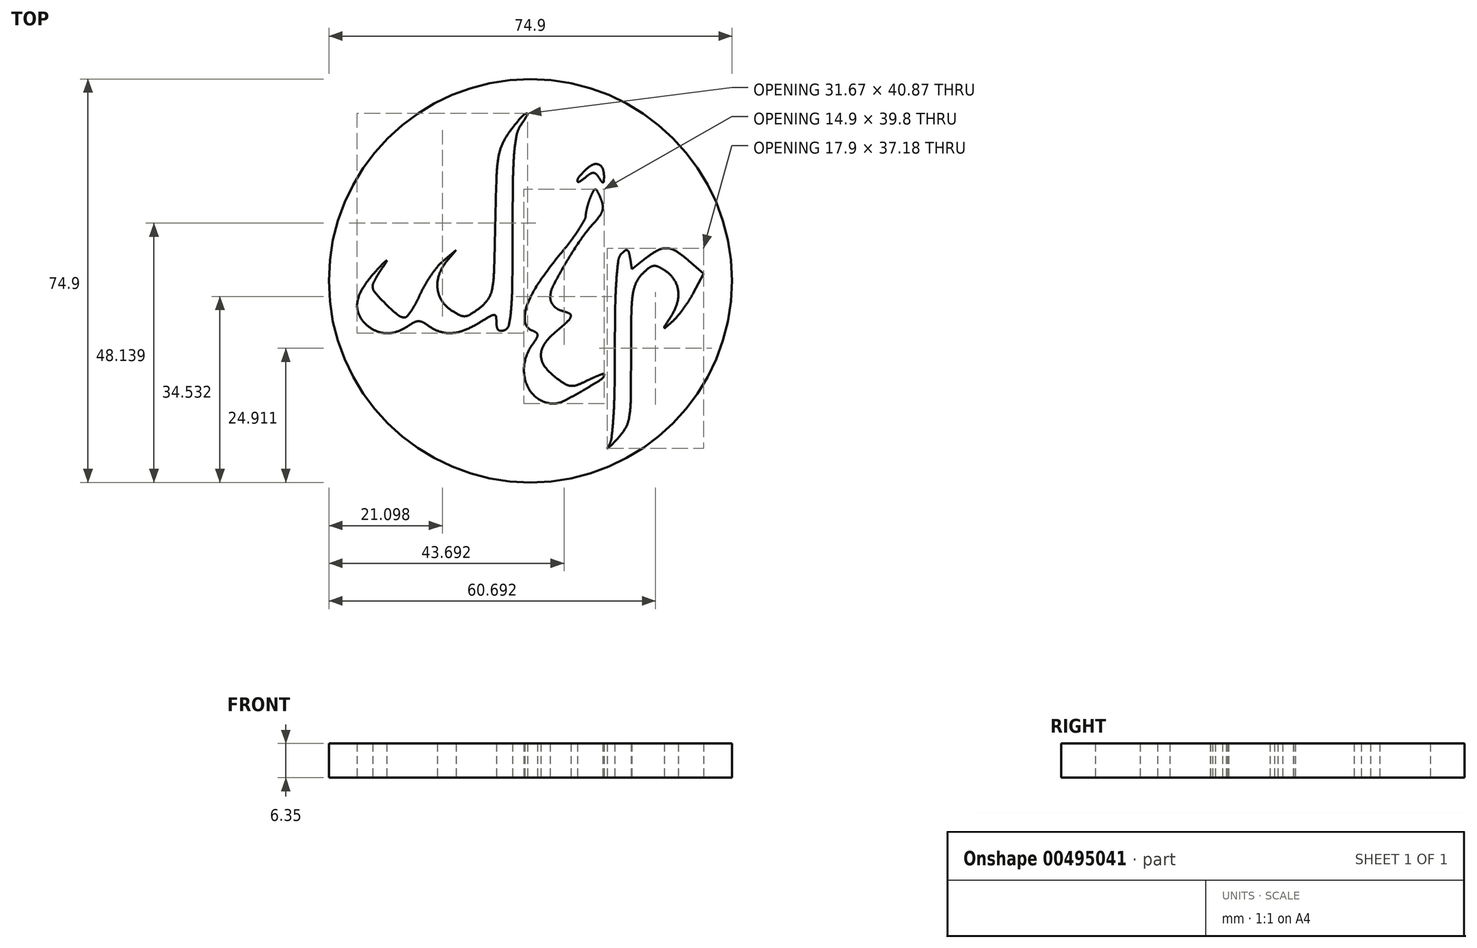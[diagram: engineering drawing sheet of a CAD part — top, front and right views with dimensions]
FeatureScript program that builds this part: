
annotation { "Feature Type Name" : "Feature", "Feature Type Description" : "" }
export const myFeature = defineFeature(function(context is Context, id is Id, definition is map)
    precondition{}
    {
        {
            var Q0;
            Q0=qCreatedBy(makeId("Top.planeOp"),FACE);
            var sketch = newSketch(context, id + "F0", { "sketchPlane" : qUnion([Q0])});
            skArc(sketch, "E0", {"start": v(-3.73, 27.88) * mm, "mid": v(-4.51, 26.73) * mm, "end": v(-5.16, 25.5) * mm});
            skArc(sketch, "E1", {"start": v(-5.16, 25.5) * mm, "mid": v(-5.63, 24.29) * mm, "end": v(-5.92, 23.03) * mm});
            skArc(sketch, "E2", {"start": v(-5.92, 23.03) * mm, "mid": v(-6.17, 21.14) * mm, "end": v(-6.3, 19.24) * mm});
            skArc(sketch, "E3", {"start": v(-6.3, 19.24) * mm, "mid": v(-6.43, 14.99) * mm, "end": v(-6.53, 10.73) * mm});
            skArc(sketch, "E4", {"start": v(-6.53, 10.73) * mm, "mid": v(-6.63, 6.2) * mm, "end": v(-6.76, 1.68) * mm});
            skArc(sketch, "E5", {"start": v(-6.76, 1.68) * mm, "mid": v(-6.88, 0.04) * mm, "end": v(-7.12, -1.59) * mm});
            skArc(sketch, "E6", {"start": v(-7.12, -1.59) * mm, "mid": v(-7.42, -2.58) * mm, "end": v(-7.92, -3.48) * mm});
            skArc(sketch, "E7", {"start": v(-7.92, -3.48) * mm, "mid": v(-8.64, -4.36) * mm, "end": v(-9.5, -5.11) * mm});
            skArc(sketch, "E8", {"start": v(-9.5, -5.11) * mm, "mid": v(-10.33, -5.7) * mm, "end": v(-11.19, -6.27) * mm});
            skArc(sketch, "E9", {"start": v(-11.19, -6.27) * mm, "mid": v(-11.66, -6.5) * mm, "end": v(-12.18, -6.59) * mm});
            skArc(sketch, "E10", {"start": v(-12.18, -6.59) * mm, "mid": v(-12.68, -6.55) * mm, "end": v(-13.15, -6.38) * mm});
            skArc(sketch, "E11", {"start": v(-13.15, -6.38) * mm, "mid": v(-13.96, -5.93) * mm, "end": v(-14.75, -5.45) * mm});
            skArc(sketch, "E12", {"start": v(-14.75, -5.45) * mm, "mid": v(-15.72, -4.65) * mm, "end": v(-16.5, -3.65) * mm});
            skArc(sketch, "E13", {"start": v(-16.5, -3.65) * mm, "mid": v(-17.02, -2.54) * mm, "end": v(-17.27, -1.33) * mm});
            skArc(sketch, "E14", {"start": v(-17.27, -1.33) * mm, "mid": v(-17.24, -0.04) * mm, "end": v(-16.94, 1.22) * mm});
            skArc(sketch, "E15", {"start": v(-16.94, 1.22) * mm, "mid": v(-16.35, 2.47) * mm, "end": v(-15.56, 3.6) * mm});
            skLineSegment(sketch, "E16", {"start": v(-15.56, 3.6) * mm, "end": v(-13.8, 5.68) * mm});
            skLineSegment(sketch, "E17", {"start": v(-13.8, 5.68) * mm, "end": v(-16.2, 3.68) * mm});
            skArc(sketch, "E18", {"start": v(-16.2, 3.68) * mm, "mid": v(-16.76, 3.18) * mm, "end": v(-17.26, 2.62) * mm});
            skArc(sketch, "E19", {"start": v(-17.26, 2.62) * mm, "mid": v(-17.87, 1.83) * mm, "end": v(-18.45, 1.02) * mm});
            skArc(sketch, "E20", {"start": v(-18.45, 1.02) * mm, "mid": v(-19.04, 0.13) * mm, "end": v(-19.6, -0.8) * mm});
            skArc(sketch, "E21", {"start": v(-19.6, -0.8) * mm, "mid": v(-20.07, -1.67) * mm, "end": v(-20.5, -2.57) * mm});
            skArc(sketch, "E22", {"start": v(-20.5, -2.57) * mm, "mid": v(-20.89, -3.39) * mm, "end": v(-21.3, -4.2) * mm});
            skArc(sketch, "E23", {"start": v(-21.3, -4.2) * mm, "mid": v(-21.7, -4.9) * mm, "end": v(-22.14, -5.57) * mm});
            skArc(sketch, "E24", {"start": v(-22.14, -5.57) * mm, "mid": v(-22.51, -6.09) * mm, "end": v(-22.9, -6.59) * mm});
            skArc(sketch, "E25", {"start": v(-22.9, -6.59) * mm, "mid": v(-23.13, -6.76) * mm, "end": v(-23.4, -6.82) * mm});
            skArc(sketch, "E26", {"start": v(-23.4, -6.82) * mm, "mid": v(-24.05, -6.7) * mm, "end": v(-24.62, -6.37) * mm});
            skArc(sketch, "E27", {"start": v(-24.62, -6.37) * mm, "mid": v(-25.74, -5.4) * mm, "end": v(-26.82, -4.37) * mm});
            skArc(sketch, "E28", {"start": v(-26.82, -4.37) * mm, "mid": v(-27.87, -3.3) * mm, "end": v(-28.86, -2.2) * mm});
            skArc(sketch, "E29", {"start": v(-28.86, -2.2) * mm, "mid": v(-29.2, -1.64) * mm, "end": v(-29.3, -1) * mm});
            skArc(sketch, "E30", {"start": v(-29.3, -1) * mm, "mid": v(-29.28, -0.73) * mm, "end": v(-29.2, -0.48) * mm});
            skArc(sketch, "E31", {"start": v(-29.2, -0.48) * mm, "mid": v(-28.95, 0) * mm, "end": v(-28.7, 0.5) * mm});
            skArc(sketch, "E32", {"start": v(-28.7, 0.5) * mm, "mid": v(-28.37, 1.07) * mm, "end": v(-28.02, 1.63) * mm});
            skArc(sketch, "E33", {"start": v(-28.02, 1.63) * mm, "mid": v(-27.63, 2.22) * mm, "end": v(-27.22, 2.8) * mm});
            skArc(sketch, "E34", {"start": v(-27.22, 2.8) * mm, "mid": v(-26.95, 3.2) * mm, "end": v(-26.7, 3.62) * mm});
            skArc(sketch, "E35", {"start": v(-26.7, 3.62) * mm, "mid": v(-26.7, 3.7) * mm, "end": v(-26.79, 3.7) * mm});
            skArc(sketch, "E36", {"start": v(-26.79, 3.7) * mm, "mid": v(-27.1, 3.46) * mm, "end": v(-27.4, 3.18) * mm});
            skArc(sketch, "E37", {"start": v(-27.4, 3.18) * mm, "mid": v(-28.07, 2.48) * mm, "end": v(-28.72, 1.77) * mm});
            skArc(sketch, "E38", {"start": v(-28.72, 1.77) * mm, "mid": v(-29.97, 0.29) * mm, "end": v(-31.1, -1.28) * mm});
            skArc(sketch, "E39", {"start": v(-31.1, -1.28) * mm, "mid": v(-31.74, -2.53) * mm, "end": v(-32.13, -3.89) * mm});
            skArc(sketch, "E40", {"start": v(-32.13, -3.89) * mm, "mid": v(-32.17, -5.03) * mm, "end": v(-31.89, -6.15) * mm});
            skArc(sketch, "E41", {"start": v(-31.89, -6.15) * mm, "mid": v(-31.3, -7.23) * mm, "end": v(-30.48, -8.16) * mm});
            skArc(sketch, "E42", {"start": v(-30.48, -8.16) * mm, "mid": v(-29.64, -8.8) * mm, "end": v(-28.71, -9.3) * mm});
            skArc(sketch, "E43", {"start": v(-28.71, -9.3) * mm, "mid": v(-27.77, -9.62) * mm, "end": v(-26.78, -9.75) * mm});
            skArc(sketch, "E44", {"start": v(-26.78, -9.75) * mm, "mid": v(-25.75, -9.69) * mm, "end": v(-24.76, -9.44) * mm});
            skArc(sketch, "E45", {"start": v(-24.76, -9.44) * mm, "mid": v(-23.72, -9) * mm, "end": v(-22.76, -8.42) * mm});
            skArc(sketch, "E46", {"start": v(-22.76, -8.42) * mm, "mid": v(-22.2, -8.05) * mm, "end": v(-21.6, -7.72) * mm});
            skArc(sketch, "E47", {"start": v(-21.6, -7.72) * mm, "mid": v(-21.2, -7.57) * mm, "end": v(-20.77, -7.52) * mm});
            skArc(sketch, "E48", {"start": v(-20.77, -7.52) * mm, "mid": v(-20.35, -7.57) * mm, "end": v(-19.95, -7.72) * mm});
            skArc(sketch, "E49", {"start": v(-19.95, -7.72) * mm, "mid": v(-19.38, -8.05) * mm, "end": v(-18.84, -8.42) * mm});
            skArc(sketch, "E50", {"start": v(-18.84, -8.42) * mm, "mid": v(-17.86, -9.02) * mm, "end": v(-16.8, -9.45) * mm});
            skArc(sketch, "E51", {"start": v(-16.8, -9.45) * mm, "mid": v(-15.74, -9.69) * mm, "end": v(-14.65, -9.72) * mm});
            skArc(sketch, "E52", {"start": v(-14.65, -9.72) * mm, "mid": v(-13.44, -9.55) * mm, "end": v(-12.27, -9.18) * mm});
            skArc(sketch, "E53", {"start": v(-12.27, -9.18) * mm, "mid": v(-10.89, -8.56) * mm, "end": v(-9.56, -7.83) * mm});
            skArc(sketch, "E54", {"start": v(-9.56, -7.83) * mm, "mid": v(-8.48, -7.18) * mm, "end": v(-7.39, -6.53) * mm});
            skArc(sketch, "E55", {"start": v(-7.39, -6.53) * mm, "mid": v(-7.07, -6.4) * mm, "end": v(-6.73, -6.35) * mm});
            skArc(sketch, "E56", {"start": v(-6.73, -6.35) * mm, "mid": v(-6.5, -6.43) * mm, "end": v(-6.4, -6.64) * mm});
            skArc(sketch, "E57", {"start": v(-6.4, -6.64) * mm, "mid": v(-6.33, -7.22) * mm, "end": v(-6.3, -7.8) * mm});
            skArc(sketch, "E58", {"start": v(-6.3, -7.8) * mm, "mid": v(-6.29, -8.22) * mm, "end": v(-6.22, -8.64) * mm});
            skArc(sketch, "E59", {"start": v(-6.22, -8.64) * mm, "mid": v(-6.12, -8.9) * mm, "end": v(-5.94, -9.13) * mm});
            skArc(sketch, "E60", {"start": v(-5.94, -9.13) * mm, "mid": v(-5.72, -9.27) * mm, "end": v(-5.47, -9.3) * mm});
            skArc(sketch, "E61", {"start": v(-5.47, -9.3) * mm, "mid": v(-5.13, -9.27) * mm, "end": v(-4.8, -9.18) * mm});
            skArc(sketch, "E62", {"start": v(-4.8, -9.18) * mm, "mid": v(-4.28, -8.8) * mm, "end": v(-4, -8.22) * mm});
            skArc(sketch, "E63", {"start": v(-4, -8.22) * mm, "mid": v(-3.75, -6.83) * mm, "end": v(-3.59, -5.42) * mm});
            skArc(sketch, "E64", {"start": v(-3.59, -5.42) * mm, "mid": v(-3.43, -3) * mm, "end": v(-3.36, -0.56) * mm});
            skArc(sketch, "E65", {"start": v(-3.36, -0.56) * mm, "mid": v(-3.32, 4.25) * mm, "end": v(-3.3, 9.07) * mm});
            skArc(sketch, "E66", {"start": v(-3.3, 9.07) * mm, "mid": v(-3.3, 13.75) * mm, "end": v(-3.25, 18.44) * mm});
            skArc(sketch, "E67", {"start": v(-3.25, 18.44) * mm, "mid": v(-3.17, 21.09) * mm, "end": v(-3, 23.73) * mm});
            skArc(sketch, "E68", {"start": v(-3, 23.73) * mm, "mid": v(-2.83, 25.4) * mm, "end": v(-2.56, 27.05) * mm});
            skArc(sketch, "E69", {"start": v(-2.56, 27.05) * mm, "mid": v(-2.26, 28.05) * mm, "end": v(-1.75, 28.96) * mm});
            skArc(sketch, "E70", {"start": v(-1.75, 28.96) * mm, "mid": v(-1.12, 29.9) * mm, "end": v(-0.54, 30.87) * mm});
            skArc(sketch, "E71", {"start": v(-0.54, 30.87) * mm, "mid": v(-0.56, 31.08) * mm, "end": v(-0.77, 31.1) * mm});
            skArc(sketch, "E72", {"start": v(-0.77, 31.1) * mm, "mid": v(-1.35, 30.72) * mm, "end": v(-1.85, 30.22) * mm});
            skArc(sketch, "E73", {"start": v(-1.85, 30.22) * mm, "mid": v(-2.8, 29.06) * mm, "end": v(-3.73, 27.88) * mm});
            skArc(sketch, "E74", {"start": v(10.27, 20.62) * mm, "mid": v(9.63, 19.95) * mm, "end": v(9, 19.26) * mm});
            skArc(sketch, "E75", {"start": v(9, 19.26) * mm, "mid": v(8.8, 18.92) * mm, "end": v(8.73, 18.53) * mm});
            skArc(sketch, "E76", {"start": v(8.73, 18.53) * mm, "mid": v(8.84, 18.35) * mm, "end": v(9.05, 18.35) * mm});
            skArc(sketch, "E77", {"start": v(9.05, 18.35) * mm, "mid": v(9.67, 18.78) * mm, "end": v(10.27, 19.25) * mm});
            skArc(sketch, "E78", {"start": v(10.27, 19.25) * mm, "mid": v(10.7, 19.58) * mm, "end": v(11.14, 19.88) * mm});
            skArc(sketch, "E79", {"start": v(11.14, 19.88) * mm, "mid": v(11.42, 20) * mm, "end": v(11.72, 20.04) * mm});
            skArc(sketch, "E80", {"start": v(11.72, 20.04) * mm, "mid": v(11.98, 19.97) * mm, "end": v(12.2, 19.81) * mm});
            skArc(sketch, "E81", {"start": v(12.2, 19.81) * mm, "mid": v(12.5, 19.48) * mm, "end": v(12.75, 19.12) * mm});
            skArc(sketch, "E82", {"start": v(12.75, 19.12) * mm, "mid": v(13, 18.73) * mm, "end": v(13.26, 18.36) * mm});
            skArc(sketch, "E83", {"start": v(13.26, 18.36) * mm, "mid": v(13.36, 18.28) * mm, "end": v(13.5, 18.28) * mm});
            skArc(sketch, "E84", {"start": v(13.5, 18.28) * mm, "mid": v(13.6, 18.34) * mm, "end": v(13.64, 18.46) * mm});
            skArc(sketch, "E85", {"start": v(13.64, 18.46) * mm, "mid": v(13.67, 18.92) * mm, "end": v(13.68, 19.37) * mm});
            skArc(sketch, "E86", {"start": v(13.68, 19.37) * mm, "mid": v(13.61, 20.12) * mm, "end": v(13.42, 20.85) * mm});
            skArc(sketch, "E87", {"start": v(13.42, 20.85) * mm, "mid": v(13.13, 21.3) * mm, "end": v(12.66, 21.6) * mm});
            skArc(sketch, "E88", {"start": v(12.66, 21.6) * mm, "mid": v(12.1, 21.69) * mm, "end": v(11.55, 21.54) * mm});
            skArc(sketch, "E89", {"start": v(11.55, 21.54) * mm, "mid": v(10.87, 21.13) * mm, "end": v(10.27, 20.62) * mm});
            skArc(sketch, "E90", {"start": v(11.2, 15.62) * mm, "mid": v(11.03, 15.2) * mm, "end": v(10.88, 14.76) * mm});
            skArc(sketch, "E91", {"start": v(10.88, 14.76) * mm, "mid": v(10.72, 14.28) * mm, "end": v(10.59, 13.8) * mm});
            skArc(sketch, "E92", {"start": v(10.59, 13.8) * mm, "mid": v(10.47, 13.33) * mm, "end": v(10.37, 12.86) * mm});
            skArc(sketch, "E93", {"start": v(10.37, 12.86) * mm, "mid": v(10.31, 12.5) * mm, "end": v(10.28, 12.12) * mm});
            skArc(sketch, "E94", {"start": v(10.28, 12.12) * mm, "mid": v(10.2, 11.67) * mm, "end": v(10.02, 11.24) * mm});
            skArc(sketch, "E95", {"start": v(10.02, 11.24) * mm, "mid": v(9.53, 10.4) * mm, "end": v(9, 9.57) * mm});
            skArc(sketch, "E96", {"start": v(9, 9.57) * mm, "mid": v(8.35, 8.59) * mm, "end": v(7.66, 7.63) * mm});
            skArc(sketch, "E97", {"start": v(7.66, 7.63) * mm, "mid": v(6.88, 6.61) * mm, "end": v(6.08, 5.62) * mm});
            skArc(sketch, "E98", {"start": v(6.08, 5.62) * mm, "mid": v(3.88, 2.86) * mm, "end": v(1.8, 0) * mm});
            skArc(sketch, "E99", {"start": v(1.8, 0) * mm, "mid": v(0.48, -2.14) * mm, "end": v(-0.57, -4.41) * mm});
            skArc(sketch, "E100", {"start": v(-0.57, -4.41) * mm, "mid": v(-0.97, -5.92) * mm, "end": v(-1.03, -7.48) * mm});
            skArc(sketch, "E101", {"start": v(-1.03, -7.48) * mm, "mid": v(-0.64, -8.53) * mm, "end": v(0.25, -9.2) * mm});
            skArc(sketch, "E102", {"start": v(0.25, -9.2) * mm, "mid": v(0.67, -9.39) * mm, "end": v(1.07, -9.62) * mm});
            skArc(sketch, "E103", {"start": v(1.07, -9.62) * mm, "mid": v(1.25, -9.81) * mm, "end": v(1.31, -10.06) * mm});
            skArc(sketch, "E104", {"start": v(1.31, -10.06) * mm, "mid": v(1.27, -10.4) * mm, "end": v(1.13, -10.7) * mm});
            skArc(sketch, "E105", {"start": v(1.13, -10.7) * mm, "mid": v(0.7, -11.37) * mm, "end": v(0.25, -12.03) * mm});
            skArc(sketch, "E106", {"start": v(0.25, -12.03) * mm, "mid": v(-0.64, -13.69) * mm, "end": v(-1.13, -15.5) * mm});
            skArc(sketch, "E107", {"start": v(-1.13, -15.5) * mm, "mid": v(-1.17, -17.34) * mm, "end": v(-0.75, -19.12) * mm});
            skArc(sketch, "E108", {"start": v(-0.75, -19.12) * mm, "mid": v(0.06, -20.6) * mm, "end": v(1.26, -21.8) * mm});
            skArc(sketch, "E109", {"start": v(1.26, -21.8) * mm, "mid": v(2.69, -22.56) * mm, "end": v(4.29, -22.82) * mm});
            skArc(sketch, "E110", {"start": v(4.29, -22.82) * mm, "mid": v(5.2, -22.7) * mm, "end": v(6.08, -22.39) * mm});
            skArc(sketch, "E111", {"start": v(6.08, -22.39) * mm, "mid": v(7.87, -21.45) * mm, "end": v(9.63, -20.46) * mm});
            skArc(sketch, "E112", {"start": v(9.63, -20.46) * mm, "mid": v(11.41, -19.4) * mm, "end": v(13.17, -18.31) * mm});
            skArc(sketch, "E113", {"start": v(13.17, -18.31) * mm, "mid": v(13.55, -17.9) * mm, "end": v(13.7, -17.36) * mm});
            skArc(sketch, "E114", {"start": v(13.7, -17.36) * mm, "mid": v(13.65, -17.28) * mm, "end": v(13.57, -17.27) * mm});
            skArc(sketch, "E115", {"start": v(13.57, -17.27) * mm, "mid": v(13.17, -17.4) * mm, "end": v(12.78, -17.54) * mm});
            skArc(sketch, "E116", {"start": v(12.78, -17.54) * mm, "mid": v(12.28, -17.74) * mm, "end": v(11.78, -17.95) * mm});
            skArc(sketch, "E117", {"start": v(11.78, -17.95) * mm, "mid": v(11.18, -18.23) * mm, "end": v(10.6, -18.52) * mm});
            skArc(sketch, "E118", {"start": v(10.6, -18.52) * mm, "mid": v(9.66, -18.96) * mm, "end": v(8.7, -19.36) * mm});
            skArc(sketch, "E119", {"start": v(8.7, -19.36) * mm, "mid": v(8.14, -19.5) * mm, "end": v(7.56, -19.53) * mm});
            skArc(sketch, "E120", {"start": v(7.56, -19.53) * mm, "mid": v(7, -19.42) * mm, "end": v(6.49, -19.19) * mm});
            skArc(sketch, "E121", {"start": v(6.49, -19.19) * mm, "mid": v(5.65, -18.66) * mm, "end": v(4.84, -18.09) * mm});
            skArc(sketch, "E122", {"start": v(4.84, -18.09) * mm, "mid": v(3.7, -17.11) * mm, "end": v(2.7, -15.99) * mm});
            skArc(sketch, "E123", {"start": v(2.7, -15.99) * mm, "mid": v(2.17, -15) * mm, "end": v(1.96, -13.9) * mm});
            skArc(sketch, "E124", {"start": v(1.96, -13.9) * mm, "mid": v(2.11, -12.78) * mm, "end": v(2.6, -11.76) * mm});
            skArc(sketch, "E125", {"start": v(2.6, -11.76) * mm, "mid": v(3.54, -10.57) * mm, "end": v(4.64, -9.51) * mm});
            skArc(sketch, "E126", {"start": v(4.64, -9.51) * mm, "mid": v(5.82, -8.5) * mm, "end": v(7, -7.47) * mm});
            skArc(sketch, "E127", {"start": v(7, -7.47) * mm, "mid": v(7.3, -7.1) * mm, "end": v(7.5, -6.64) * mm});
            skArc(sketch, "E128", {"start": v(7.5, -6.64) * mm, "mid": v(7.47, -6.3) * mm, "end": v(7.22, -6.06) * mm});
            skArc(sketch, "E129", {"start": v(7.22, -6.06) * mm, "mid": v(6.46, -5.76) * mm, "end": v(5.7, -5.53) * mm});
            skArc(sketch, "E130", {"start": v(5.7, -5.53) * mm, "mid": v(5.3, -5.39) * mm, "end": v(4.92, -5.18) * mm});
            skArc(sketch, "E131", {"start": v(4.92, -5.18) * mm, "mid": v(4.57, -4.92) * mm, "end": v(4.27, -4.6) * mm});
            skArc(sketch, "E132", {"start": v(4.27, -4.6) * mm, "mid": v(4.03, -4.26) * mm, "end": v(3.84, -3.88) * mm});
            skArc(sketch, "E133", {"start": v(3.84, -3.88) * mm, "mid": v(3.73, -3.5) * mm, "end": v(3.7, -3.1) * mm});
            skArc(sketch, "E134", {"start": v(3.7, -3.1) * mm, "mid": v(3.82, -2) * mm, "end": v(4.2, -0.97) * mm});
            skArc(sketch, "E135", {"start": v(4.2, -0.97) * mm, "mid": v(5.36, 1.18) * mm, "end": v(6.57, 3.3) * mm});
            skArc(sketch, "E136", {"start": v(6.57, 3.3) * mm, "mid": v(7.92, 5.51) * mm, "end": v(9.35, 7.67) * mm});
            skArc(sketch, "E137", {"start": v(9.35, 7.67) * mm, "mid": v(10.6, 9.34) * mm, "end": v(11.95, 10.92) * mm});
            skArc(sketch, "E138", {"start": v(11.95, 10.92) * mm, "mid": v(12.47, 11.51) * mm, "end": v(12.94, 12.14) * mm});
            skArc(sketch, "E139", {"start": v(12.94, 12.14) * mm, "mid": v(13.2, 12.62) * mm, "end": v(13.39, 13.15) * mm});
            skArc(sketch, "E140", {"start": v(13.39, 13.15) * mm, "mid": v(13.45, 13.65) * mm, "end": v(13.4, 14.15) * mm});
            skArc(sketch, "E141", {"start": v(13.4, 14.15) * mm, "mid": v(13.25, 14.76) * mm, "end": v(13.03, 15.35) * mm});
            skArc(sketch, "E142", {"start": v(13.03, 15.35) * mm, "mid": v(12.7, 16.06) * mm, "end": v(12.38, 16.75) * mm});
            skArc(sketch, "E143", {"start": v(12.38, 16.75) * mm, "mid": v(12.25, 16.9) * mm, "end": v(12.07, 16.98) * mm});
            skArc(sketch, "E144", {"start": v(12.07, 16.98) * mm, "mid": v(11.89, 16.95) * mm, "end": v(11.76, 16.82) * mm});
            skArc(sketch, "E145", {"start": v(11.76, 16.82) * mm, "mid": v(11.48, 16.22) * mm, "end": v(11.2, 15.62) * mm});
            skArc(sketch, "E146", {"start": v(16.94, 5.05) * mm, "mid": v(16.53, 4.47) * mm, "end": v(16.33, 3.8) * mm});
            skArc(sketch, "E147", {"start": v(16.33, 3.8) * mm, "mid": v(16.13, 2.04) * mm, "end": v(15.98, 0.28) * mm});
            skArc(sketch, "E148", {"start": v(15.98, 0.28) * mm, "mid": v(15.83, -2.3) * mm, "end": v(15.75, -4.88) * mm});
            skArc(sketch, "E149", {"start": v(15.75, -4.88) * mm, "mid": v(15.7, -8.78) * mm, "end": v(15.7, -12.69) * mm});
            skArc(sketch, "E150", {"start": v(15.7, -12.69) * mm, "mid": v(15.67, -16.55) * mm, "end": v(15.62, -20.4) * mm});
            skArc(sketch, "E151", {"start": v(15.62, -20.4) * mm, "mid": v(15.54, -23.04) * mm, "end": v(15.4, -25.67) * mm});
            skArc(sketch, "E152", {"start": v(15.4, -25.67) * mm, "mid": v(15.24, -27.5) * mm, "end": v(15.04, -29.34) * mm});
            skArc(sketch, "E153", {"start": v(15.04, -29.34) * mm, "mid": v(14.84, -30.1) * mm, "end": v(14.44, -30.8) * mm});
            skArc(sketch, "E154", {"start": v(14.44, -30.8) * mm, "mid": v(14.36, -30.93) * mm, "end": v(14.3, -31.07) * mm});
            skArc(sketch, "E155", {"start": v(14.3, -31.07) * mm, "mid": v(14.31, -31.12) * mm, "end": v(14.37, -31.12) * mm});
            skArc(sketch, "E156", {"start": v(14.37, -31.12) * mm, "mid": v(14.66, -30.87) * mm, "end": v(14.95, -30.6) * mm});
            skArc(sketch, "E157", {"start": v(14.95, -30.6) * mm, "mid": v(15.45, -30.1) * mm, "end": v(15.94, -29.6) * mm});
            skArc(sketch, "E158", {"start": v(15.94, -29.6) * mm, "mid": v(16.8, -28.61) * mm, "end": v(17.56, -27.53) * mm});
            skArc(sketch, "E159", {"start": v(17.56, -27.53) * mm, "mid": v(18.04, -26.53) * mm, "end": v(18.33, -25.46) * mm});
            skArc(sketch, "E160", {"start": v(18.33, -25.46) * mm, "mid": v(18.55, -23.85) * mm, "end": v(18.63, -22.23) * mm});
            skArc(sketch, "E161", {"start": v(18.63, -22.23) * mm, "mid": v(18.68, -18.01) * mm, "end": v(18.7, -13.8) * mm});
            skArc(sketch, "E162", {"start": v(18.7, -13.8) * mm, "mid": v(18.7, -9.95) * mm, "end": v(18.75, -6.1) * mm});
            skArc(sketch, "E163", {"start": v(18.75, -6.1) * mm, "mid": v(18.83, -4.32) * mm, "end": v(19.02, -2.55) * mm});
            skArc(sketch, "E164", {"start": v(19.02, -2.55) * mm, "mid": v(19.25, -1.46) * mm, "end": v(19.63, -0.4) * mm});
            skArc(sketch, "E165", {"start": v(19.63, -0.4) * mm, "mid": v(20.12, 0.48) * mm, "end": v(20.76, 1.26) * mm});
            skArc(sketch, "E166", {"start": v(20.76, 1.26) * mm, "mid": v(21.38, 1.84) * mm, "end": v(22.02, 2.39) * mm});
            skArc(sketch, "E167", {"start": v(22.02, 2.39) * mm, "mid": v(22.41, 2.63) * mm, "end": v(22.85, 2.76) * mm});
            skArc(sketch, "E168", {"start": v(22.85, 2.76) * mm, "mid": v(23.3, 2.76) * mm, "end": v(23.72, 2.63) * mm});
            skArc(sketch, "E169", {"start": v(23.72, 2.63) * mm, "mid": v(24.38, 2.28) * mm, "end": v(25.01, 1.9) * mm});
            skArc(sketch, "E170", {"start": v(25.01, 1.9) * mm, "mid": v(25.92, 1.16) * mm, "end": v(26.66, 0.25) * mm});
            skArc(sketch, "E171", {"start": v(26.66, 0.25) * mm, "mid": v(27.17, -0.73) * mm, "end": v(27.44, -1.8) * mm});
            skArc(sketch, "E172", {"start": v(27.44, -1.8) * mm, "mid": v(27.47, -3) * mm, "end": v(27.25, -4.16) * mm});
            skArc(sketch, "E173", {"start": v(27.25, -4.16) * mm, "mid": v(26.77, -5.43) * mm, "end": v(26.11, -6.62) * mm});
            skArc(sketch, "E174", {"start": v(26.11, -6.62) * mm, "mid": v(25.5, -7.58) * mm, "end": v(24.89, -8.54) * mm});
            skArc(sketch, "E175", {"start": v(24.89, -8.54) * mm, "mid": v(24.85, -8.64) * mm, "end": v(24.86, -8.75) * mm});
            skArc(sketch, "E176", {"start": v(24.86, -8.75) * mm, "mid": v(24.9, -8.8) * mm, "end": v(24.98, -8.78) * mm});
            skArc(sketch, "E177", {"start": v(24.98, -8.78) * mm, "mid": v(25.69, -8.16) * mm, "end": v(26.4, -7.54) * mm});
            skArc(sketch, "E178", {"start": v(26.4, -7.54) * mm, "mid": v(26.86, -7.1) * mm, "end": v(27.3, -6.61) * mm});
            skArc(sketch, "E179", {"start": v(27.3, -6.61) * mm, "mid": v(27.84, -5.94) * mm, "end": v(28.37, -5.25) * mm});
            skArc(sketch, "E180", {"start": v(28.37, -5.25) * mm, "mid": v(28.9, -4.48) * mm, "end": v(29.42, -3.7) * mm});
            skArc(sketch, "E181", {"start": v(29.42, -3.7) * mm, "mid": v(29.87, -2.97) * mm, "end": v(30.3, -2.22) * mm});
            skLineSegment(sketch, "E182", {"start": v(30.3, -2.22) * mm, "end": v(32.2, 1.33) * mm});
            skLineSegment(sketch, "E183", {"start": v(32.2, 1.33) * mm, "end": v(29.38, 3.76) * mm});
            skArc(sketch, "E184", {"start": v(29.38, 3.76) * mm, "mid": v(28.26, 4.67) * mm, "end": v(27.07, 5.5) * mm});
            skArc(sketch, "E185", {"start": v(27.07, 5.5) * mm, "mid": v(26.25, 5.88) * mm, "end": v(25.35, 6.05) * mm});
            skArc(sketch, "E186", {"start": v(25.35, 6.05) * mm, "mid": v(24.47, 5.97) * mm, "end": v(23.65, 5.66) * mm});
            skArc(sketch, "E187", {"start": v(23.65, 5.66) * mm, "mid": v(22.5, 4.96) * mm, "end": v(21.4, 4.17) * mm});
            skLineSegment(sketch, "E188", {"start": v(21.4, 4.17) * mm, "end": v(18.83, 2.15) * mm});
            skLineSegment(sketch, "E189", {"start": v(18.83, 2.15) * mm, "end": v(18.51, 4.23) * mm});
            skArc(sketch, "E190", {"start": v(18.51, 4.23) * mm, "mid": v(18.42, 4.76) * mm, "end": v(18.3, 5.28) * mm});
            skArc(sketch, "E191", {"start": v(18.3, 5.28) * mm, "mid": v(18.2, 5.5) * mm, "end": v(18, 5.65) * mm});
            skArc(sketch, "E192", {"start": v(18, 5.65) * mm, "mid": v(17.8, 5.69) * mm, "end": v(17.6, 5.61) * mm});
            skArc(sketch, "E193", {"start": v(17.6, 5.61) * mm, "mid": v(17.26, 5.34) * mm, "end": v(16.94, 5.05) * mm});
            skPoint(sketch, "E194", {"position": v(0, 0) * mm});
            skCircle(sketch, "E195", {"center": v(0, 0) * mm, "radius": 37.45 * mm});
            skSolve(sketch);
        }
        {
            var Q0;
            Q0=makeQuery(id+"F0.imprint","IMPRINT",FACE,{"disambiguationData":[TD([[makeQuery(id+"F0.imprint","IMPRINT",EDGE,{"derivedFrom":sQuery(id+"F0.wireOp",EDGE,"E0")}),-1.0]])]});
            extrude(context, id + "F1", {"entities" : qUnion([Q0]), "depth" : 6.35 * mm, "offsetDistance" : 25.4 * mm});
        }
    });
